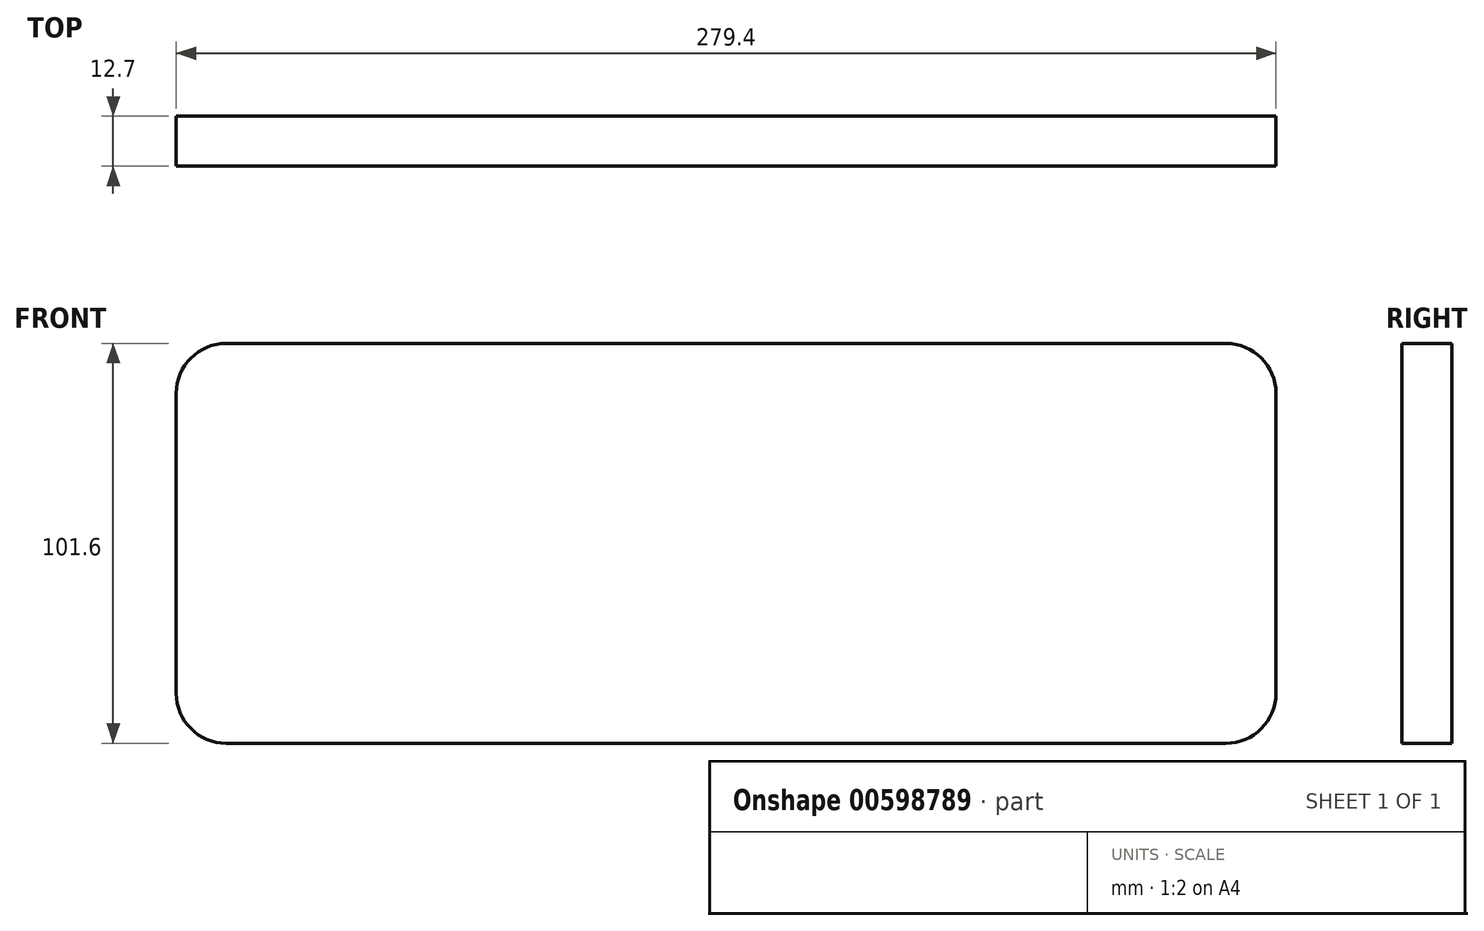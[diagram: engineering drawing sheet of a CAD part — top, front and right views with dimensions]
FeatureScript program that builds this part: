
annotation { "Feature Type Name" : "Feature", "Feature Type Description" : "" }
export const myFeature = defineFeature(function(context is Context, id is Id, definition is map)
    precondition{}
    {
        {
            var Q0;
            Q0=qCreatedBy(makeId("Front.planeOp"),FACE);
            var sketch = newSketch(context, id + "F0", { "sketchPlane" : qUnion([Q0])});
            skLineSegment(sketch, "E0", {"start": v(0, 0) * mm, "end": v(-279.4, 0) * mm});
            skLineSegment(sketch, "E1", {"start": v(-279.4, 0) * mm, "end": v(-279.4, 101.6) * mm});
            skLineSegment(sketch, "E2", {"start": v(-279.4, 101.6) * mm, "end": v(0, 101.6) * mm});
            skLineSegment(sketch, "E3", {"start": v(0, 101.6) * mm, "end": v(0, 0) * mm});
            skSolve(sketch);
        }
        {
            var Q0;
            Q0=makeQuery(id+"F0.imprint","IMPRINT",FACE,{"disambiguationData":[TD([[makeQuery(id+"F0.imprint","IMPRINT",EDGE,{"derivedFrom":sQuery(id+"F0.wireOp",EDGE,"E0")}),-1.0]])]});
            extrude(context, id + "F1", {"entities" : qUnion([Q0]), "depth" : 12.7 * mm, "offsetDistance" : 25.4 * mm});
        }
        {
            var Q0;
            Q0=makeQuery(id+"F1.opExtrude","SWEPT_EDGE",EDGE,{"disambiguationData":[OSD([sQuery(id+"F0.wireOp",EDGE,"E2"),sQuery(id+"F0.wireOp",EDGE,"E3")])]});
            var Q1;
            Q1=makeQuery(id+"F1.opExtrude","SWEPT_EDGE",EDGE,{"disambiguationData":[OSD([sQuery(id+"F0.wireOp",EDGE,"E0"),sQuery(id+"F0.wireOp",EDGE,"E3")])]});
            var Q2;
            Q2=makeQuery(id+"F1.opExtrude","SWEPT_EDGE",EDGE,{"disambiguationData":[OSD([sQuery(id+"F0.wireOp",EDGE,"E1"),sQuery(id+"F0.wireOp",EDGE,"E2")])]});
            var Q3;
            Q3=makeQuery(id+"F1.opExtrude","SWEPT_EDGE",EDGE,{"disambiguationData":[OSD([sQuery(id+"F0.wireOp",EDGE,"E0"),sQuery(id+"F0.wireOp",EDGE,"E1")])]});
            fillet(context, id + "F2", {"entities" : qUnion([Q0, Q1, Q2, Q3]), "radius" : 12.7 * mm, "tangentPropagation" : true, "allowEdgeOverflow" : false});
        }
    });
